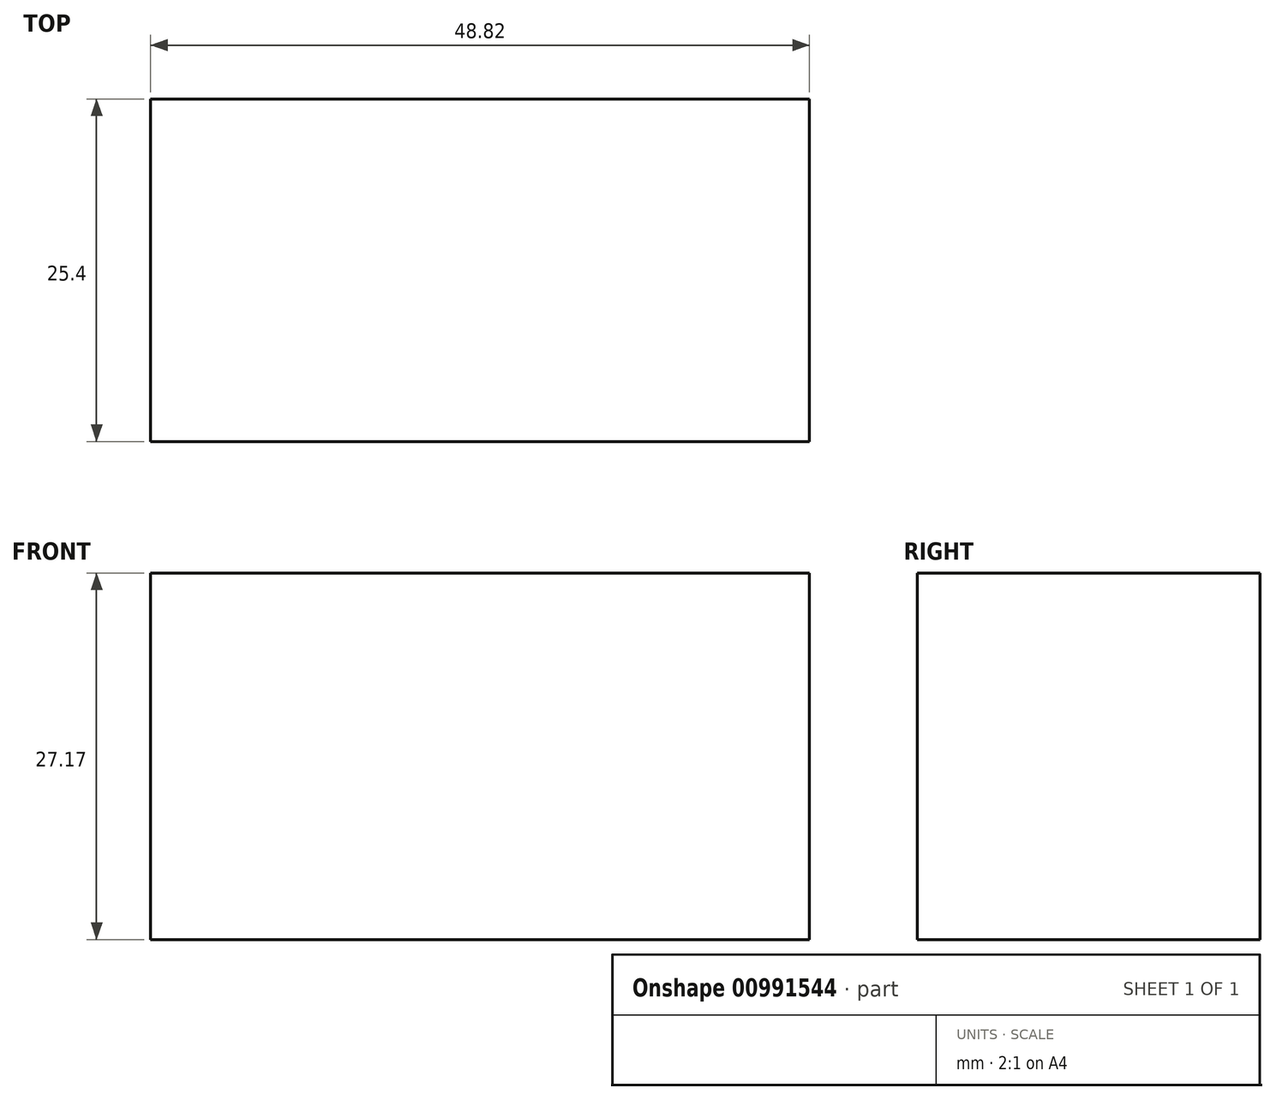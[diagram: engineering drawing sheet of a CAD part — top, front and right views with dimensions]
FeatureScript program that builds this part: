
annotation { "Feature Type Name" : "Feature", "Feature Type Description" : "" }
export const myFeature = defineFeature(function(context is Context, id is Id, definition is map)
    precondition{}
    {
        {
            var Q0;
            Q0=qCreatedBy(makeId("Front.planeOp"),FACE);
            var sketch = newSketch(context, id + "F0", { "sketchPlane" : qUnion([Q0])});
            skLineSegment(sketch, "E0.bottom", {"start": v(-58.26, 39.26) * mm, "end": v(-9.44, 39.26) * mm});
            skLineSegment(sketch, "E0.top", {"start": v(-58.26, 12.1) * mm, "end": v(-9.44, 12.1) * mm});
            skLineSegment(sketch, "E0.left", {"start": v(-58.26, 39.26) * mm, "end": v(-58.26, 12.1) * mm});
            skLineSegment(sketch, "E0.right", {"start": v(-9.44, 39.26) * mm, "end": v(-9.44, 12.1) * mm});
            skSolve(sketch);
        }
        {
            var Q0;
            Q0 = qSketchRegion(id + "F0", true);
            extrude(context, id + "F1", {"entities" : qUnion([Q0]), "depth" : 25.4 * mm, "offsetDistance" : 25.4 * mm});
        }
    });
